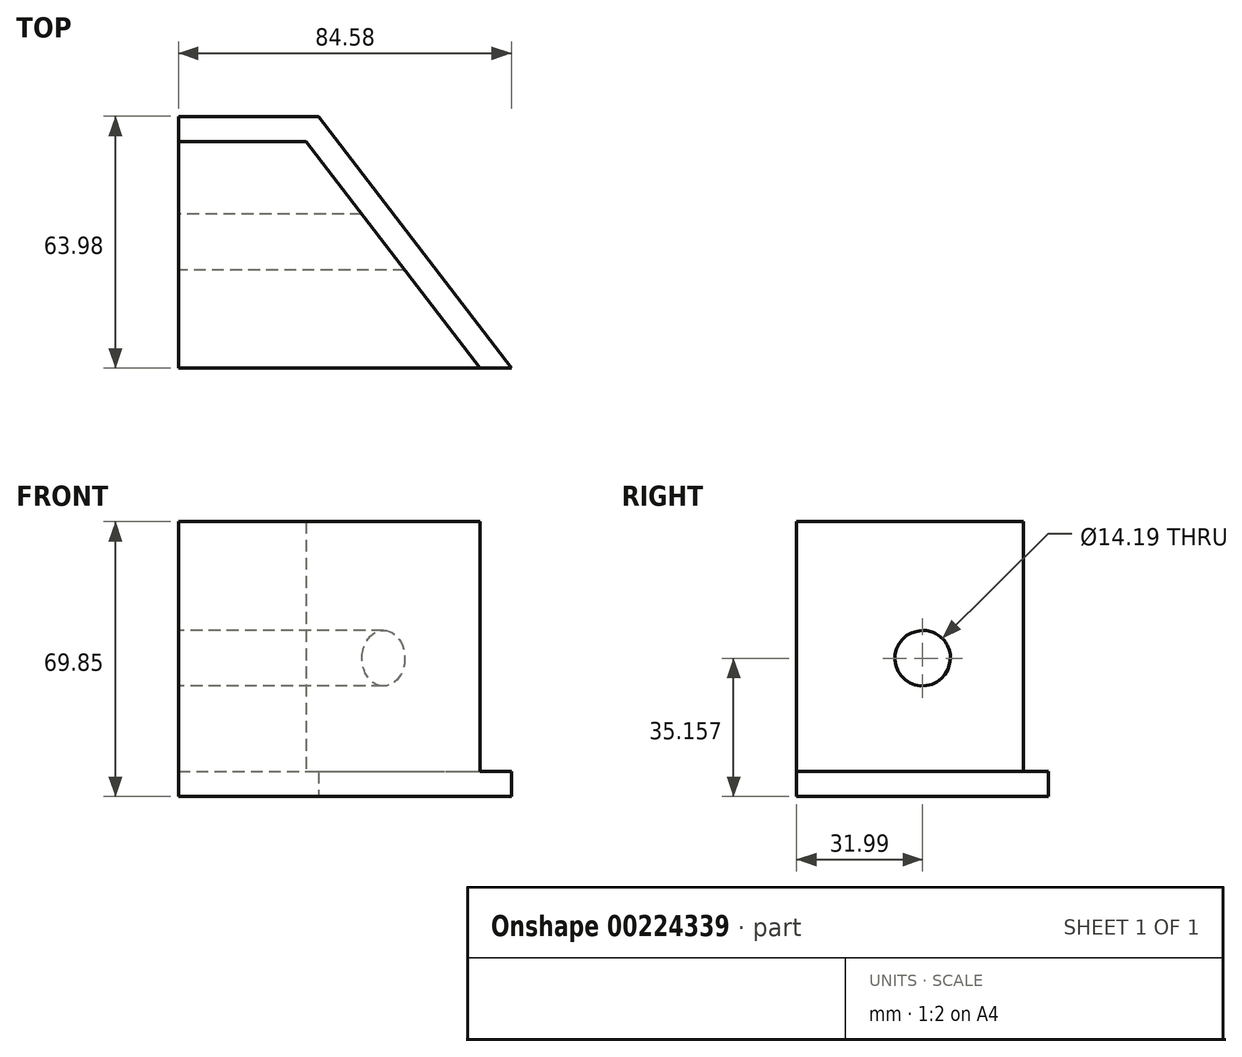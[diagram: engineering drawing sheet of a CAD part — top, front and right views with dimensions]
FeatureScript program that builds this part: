
annotation { "Feature Type Name" : "Feature", "Feature Type Description" : "" }
export const myFeature = defineFeature(function(context is Context, id is Id, definition is map)
    precondition{}
    {
        {
            var Q0;
            Q0=qCreatedBy(makeId("Top.planeOp"),FACE);
            var sketch = newSketch(context, id + "F0", { "sketchPlane" : qUnion([Q0])});
            skLineSegment(sketch, "E0.bottom", {"start": v(-42.3, 31.99) * mm, "end": v(-6.7, 31.99) * mm});
            skLineSegment(sketch, "E0.top", {"start": v(-42.3, -31.99) * mm, "end": v(42.3, -31.99) * mm});
            skLineSegment(sketch, "E0.left", {"start": v(-42.3, 31.99) * mm, "end": v(-42.3, -31.99) * mm});
            skPoint(sketch, "E0.middle", {"position": v(0, 0) * mm});
            skLineSegment(sketch, "E1", {"start": v(-6.7, 31.99) * mm, "end": v(42.3, -31.99) * mm});
            skPoint(sketch, "E0.right.start.orphan", {"position": v(42.3, 31.99) * mm});
            skSolve(sketch);
        }
        {
            var Q0;
            Q0 = qSketchRegion(id + "F0", true);
            extrude(context, id + "F1", {"entities" : qUnion([Q0]), "depth" : 6.35 * mm});
        }
        {
            var Q0;
            Q0=makeQuery(id+"F1.opExtrude","CAP_FACE",FACE,{"disambiguationData":[OSD([sQuery(id+"F0.wireOp",EDGE,"E0.bottom"),sQuery(id+"F0.wireOp",EDGE,"E0.top"),sQuery(id+"F0.wireOp",EDGE,"E0.left"),sQuery(id+"F0.wireOp",EDGE,"E1")])],"isStart":false});
            var sketch = newSketch(context, id + "F2", { "sketchPlane" : qUnion([Q0])});
            skLineSegment(sketch, "E2", {"start": v(-42.3, 25.64) * mm, "end": v(-9.83, 25.64) * mm});
            skLineSegment(sketch, "E3", {"start": v(-9.83, 25.64) * mm, "end": v(34.3, -31.99) * mm});
            skSolve(sketch);
        }
        {
            var Q0;
            {var subQ0=sQuery(id+"F2.wireOp",EDGE,"E2");Q0=makeQuery(id+"F2.imprint","IMPRINT",FACE,{"disambiguationData":[TD([[makeQuery(id+"F2.imprint","IMPRINT",EDGE,{"derivedFrom":subQ0}),-1.0]])]});}
            extrude(context, id + "F3", {"entities" : qUnion([Q0]), "operationType" : NewBodyOperationType.ADD, "depth" : 63.5 * mm});
        }
        {
            var Q0;
            {var subQ0=sQuery(id+"F0.wireOp",EDGE,"E0.left");Q0=makeQuery(id+"F3.boolean.opBoolean","MERGE",FACE,{"derivedFrom":[makeQuery(id+"F1.opExtrude","SWEPT_FACE",FACE,{"disambiguationData":[OSD([subQ0])]}),makeQuery(id+"F3.opExtrude","SWEPT_FACE",FACE,{"disambiguationData":[OSD([subQ0])]})]});}
            var sketch = newSketch(context, id + "F4", { "sketchPlane" : qUnion([Q0])});
            skCircle(sketch, "E4", {"center": v(0, 35.16) * mm, "radius": 7.1 * mm});
            skSolve(sketch);
        }
        {
            var Q0;
            Q0=makeQuery(id+"F4.imprint","IMPRINT",FACE,{"disambiguationData":[TD([[makeQuery(id+"F4.imprint","IMPRINT",EDGE,{"derivedFrom":sQuery(id+"F4.wireOp",EDGE,"E4")}),1.0]])]});
            extrude(context, id + "F5", {"entities" : qUnion([Q0]), "operationType" : NewBodyOperationType.REMOVE, "oppositeDirection" : true, "depth" : 159 * mm});
        }
    });
